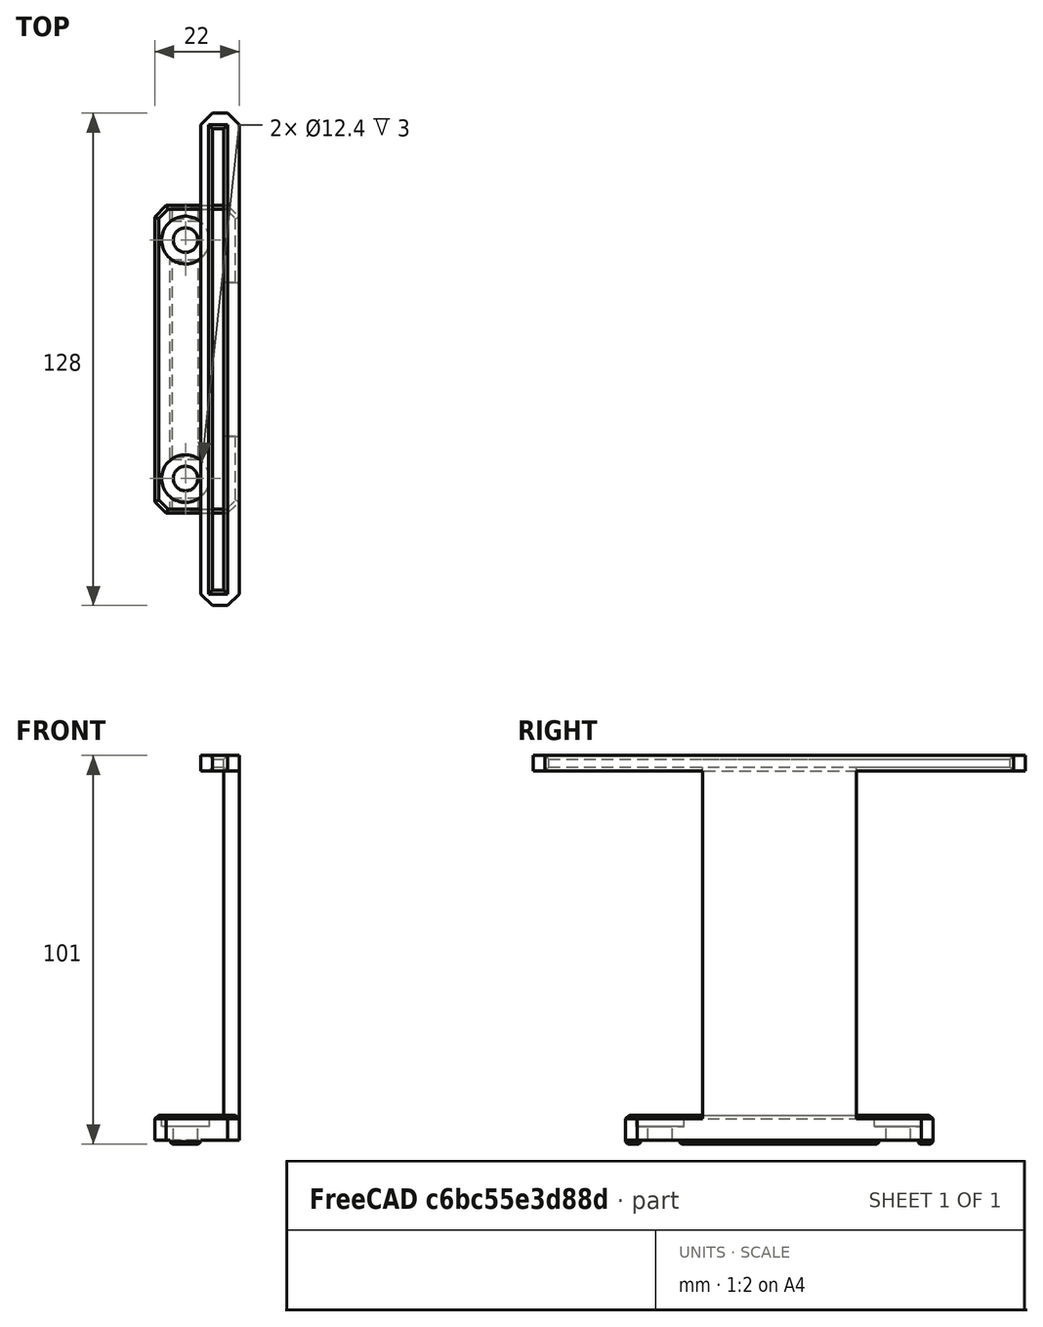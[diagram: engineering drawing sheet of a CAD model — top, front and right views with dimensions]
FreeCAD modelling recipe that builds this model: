
FCSTD DOCUMENT  (FreeCAD 0.19R24366 (Git))
Label: cable-support2
License: All rights reserved
LicenseURL: http://en.wikipedia.org/wiki/All_rights_reserved
objects: Part::Box×7, Part::Fuse×5, Part::Cut×5, Part::Cylinder×4, Part::Chamfer×4
note: 25 computed .brp shape members not serialized (recipe doc carries the construction recipe); baked Part::Feature solids carry a one-line shape summary decoded from their .brp

FEATURE [Part::Box] Box  label="Cube"
  AttacherType = Attacher::AttachEngine3D
  Height = 6.5
  Length = 22
  Placement = pos=(2,0,0) rot=(0,0,1;0rad)
  Width = 80
FEATURE [Part::Box] Box001  label="Cube001"
  AttacherType = Attacher::AttachEngine3D
  Height = 1
  Length = 8
  Placement = pos=(6,0,-1) rot=(0,0,1;0rad)
  Width = 4
FEATURE [Part::Box] Box002  label="Cube002"
  AttacherType = Attacher::AttachEngine3D
  Height = 1
  Length = 8
  Placement = pos=(6,76,-1) rot=(0,0,1;0rad)
  Width = 4
FEATURE [Part::Box] Box003  label="Cube003"
  AttacherType = Attacher::AttachEngine3D
  Height = 1
  Length = 8
  Placement = pos=(6,14,-1) rot=(0,0,1;0rad)
  Width = 52
FEATURE [Part::Cylinder] Cylinder
  Angle = 360
  AttacherType = Attacher::AttachEngine3D
  Height = 6.5
  Placement = pos=(10,9,-3) rot=(0,0,1;0rad)
  Radius = 3.2
FEATURE [Part::Cylinder] Cylinder001
  Angle = 360
  AttacherType = Attacher::AttachEngine3D
  Height = 6.5
  Placement = pos=(10,71,-3) rot=(0,0,1;0rad)
  Radius = 3.2
FEATURE [Part::Fuse] Fusion010
  Base = -> Box001
  Tool = -> Box002
FEATURE [Part::Fuse] Fusion011
  Base = -> Box003
  Tool = -> Fusion010
FEATURE [Part::Cylinder] Cylinder009
  Angle = 360
  AttacherType = Attacher::AttachEngine3D
  Height = 3
  Placement = pos=(10,9,3.5) rot=(0,0,1;0rad)
  Radius = 6.2
FEATURE [Part::Cylinder] Cylinder010
  Angle = 360
  AttacherType = Attacher::AttachEngine3D
  Height = 3
  Placement = pos=(10,71,3.5) rot=(0,0,1;0rad)
  Radius = 6.2
FEATURE [Part::Cut] Cut
  Base = -> Box
  Tool = -> Cylinder
FEATURE [Part::Cut] Cut002
  Base = -> Cut
  Tool = -> Cylinder001
FEATURE [Part::Cut] Cut003
  Base = -> Cut002
  Tool = -> Cylinder009
FEATURE [Part::Cut] Cut004
  Base = -> Cut003
  Tool = -> Cylinder010
FEATURE [Part::Box] Box004  label="Cube004"
  AttacherType = Attacher::AttachEngine3D
  Height = 100
  Length = 4
  Placement = pos=(20,20,0) rot=(0,0,1;0rad)
  Width = 40
FEATURE [Part::Fuse] Fusion
  Base = -> Fusion011
  Tool = -> Cut004
FEATURE [Part::Box] Box005  label="Cube005"
  AttacherType = Attacher::AttachEngine3D
  Height = 4
  Length = 10
  Placement = pos=(14,-24,96) rot=(0,0,1;0rad)
  Width = 128
FEATURE [Part::Box] Box006  label="Cube006"
  AttacherType = Attacher::AttachEngine3D
  Height = 4
  Length = 3
  Placement = pos=(17,-20,96) rot=(0,0,1;0rad)
  Width = 120
FEATURE [Part::Fuse] Fusion012
  Base = -> Box004
  Tool = -> Box005
FEATURE [Part::Cut] Cut005
  Base = -> Fusion012
  Tool = -> Box006
FEATURE [Part::Fuse] Fusion013
  Base = -> Fusion
  Tool = -> Cut005
FEATURE [Part::Chamfer] Chamfer
  Base = -> Fusion013
  Edges = 8 edges r=3: [Edge1,Edge3,Edge8,Edge21,Edge102,Edge109,Edge111,Edge113]
FEATURE [Part::Chamfer] Chamfer001
  Base = -> Chamfer
  Edges = 11 edges r=1: [Edge103,Edge104,Edge105,Edge106,Edge107,Edge111,Edge112,Edge113,Edge125,Edge130,Edge133]
FEATURE [Part::Chamfer] Chamfer002
  Base = -> Chamfer001
  Edges = 9 edges r=1: [Edge35,Edge36,Edge37,Edge38,Edge39,Edge40,Edge41,Edge44,Edge45]
FEATURE [Part::Chamfer] Chamfer003
  Base = -> Chamfer002
  Edges = 12 edges r=0.6: [Edge155,Edge156,Edge159,Edge162,Edge163,Edge166,Edge170,Edge171,Edge174,Edge175,Edge185,Edge186]
